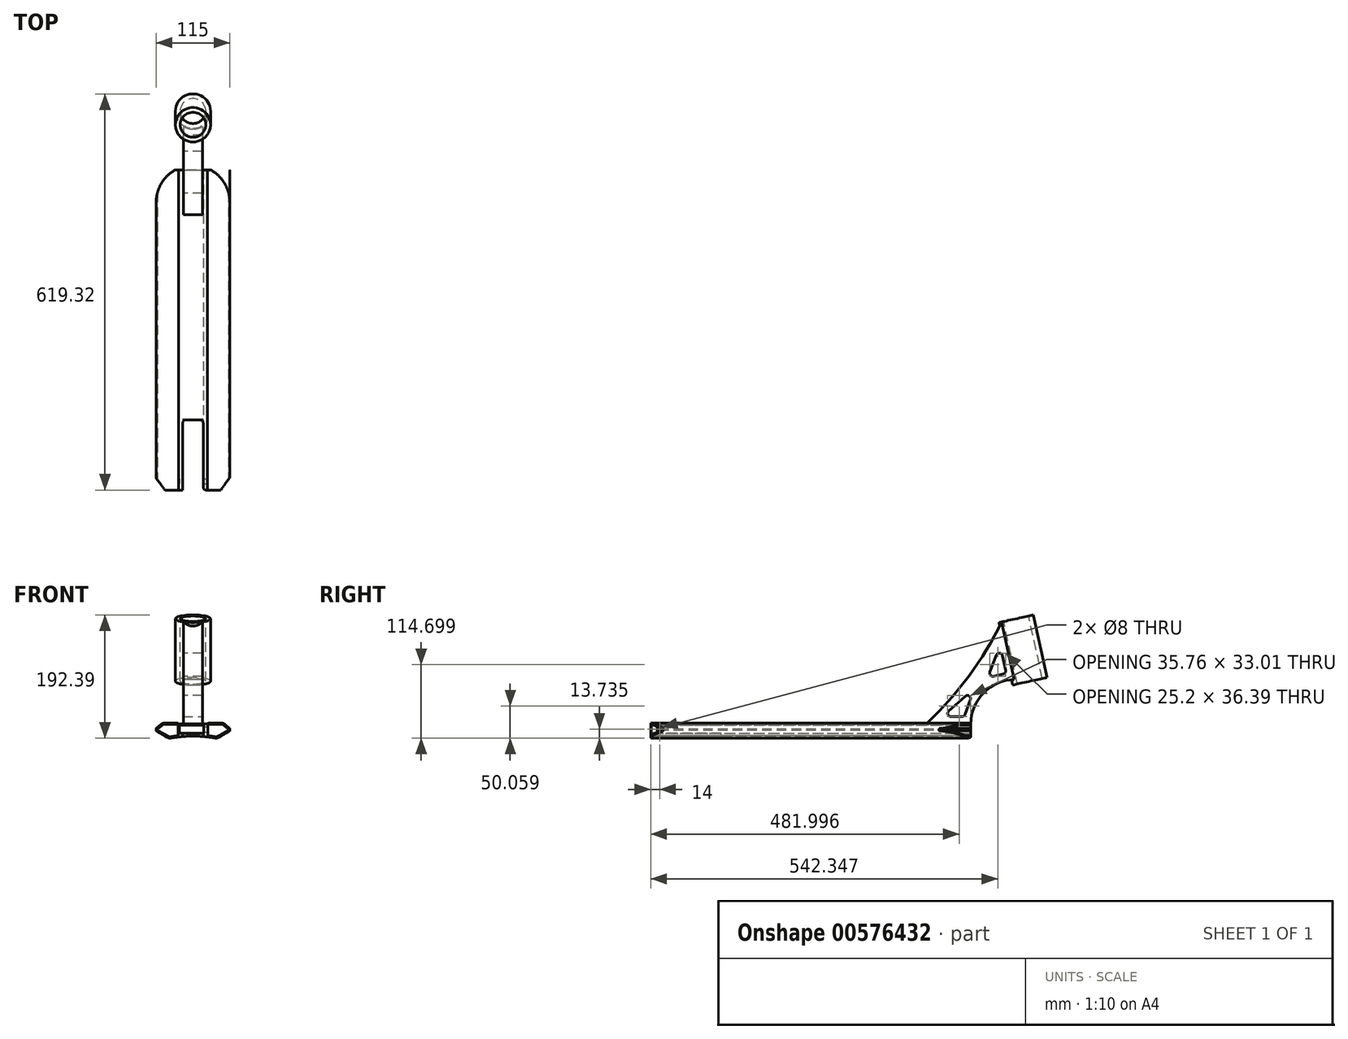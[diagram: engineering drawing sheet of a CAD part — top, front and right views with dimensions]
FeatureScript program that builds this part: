
annotation { "Feature Type Name" : "Feature", "Feature Type Description" : "" }
export const myFeature = defineFeature(function(context is Context, id is Id, definition is map)
    precondition{}
    {
        {
            var Q0;
            Q0=qCreatedBy(makeId("Front.planeOp"),FACE);
            var sketch = newSketch(context, id + "F0", { "sketchPlane" : qUnion([Q0])});
            skLineSegment(sketch, "E0", {"start": v(0, 30.17) * mm, "end": v(0, 3.52) * mm});
            skLineSegment(sketch, "E1", {"start": v(0, 21.17) * mm, "end": v(22.5, 21.17) * mm});
            skLineSegment(sketch, "E2", {"start": v(22.5, 21.17) * mm, "end": v(22.5, 22.47) * mm});
            skLineSegment(sketch, "E3", {"start": v(22.5, 22.47) * mm, "end": v(47.5, 22.47) * mm});
            skLineSegment(sketch, "E4", {"start": v(47.5, 22.47) * mm, "end": v(57.5, 14.08) * mm});
            skLineSegment(sketch, "E5", {"start": v(57.5, 14.08) * mm, "end": v(57.5, 10.08) * mm});
            skLineSegment(sketch, "E6", {"start": v(57.5, 10.08) * mm, "end": v(37.4, -1.53) * mm});
            skLineSegment(sketch, "E7.MirrorCS", {"start": v(0, 21.17) * mm, "end": v(-22.5, 21.17) * mm});
            skLineSegment(sketch, "E8.MirrorCS", {"start": v(-22.5, 22.47) * mm, "end": v(-47.5, 22.47) * mm});
            skLineSegment(sketch, "E9.MirrorCS", {"start": v(-47.5, 22.47) * mm, "end": v(-57.5, 14.08) * mm});
            skLineSegment(sketch, "E10.MirrorCS", {"start": v(-57.5, 14.08) * mm, "end": v(-57.5, 10.08) * mm});
            skLineSegment(sketch, "E11.MirrorCS", {"start": v(-57.5, 10.08) * mm, "end": v(-37.4, -1.53) * mm});
            skLineSegment(sketch, "E12.MirrorCS", {"start": v(-22.5, 21.17) * mm, "end": v(-22.5, 22.47) * mm});
            skArc(sketch, "E13", {"start": v(37.4, -1.53) * mm, "mid": v(0, 2) * mm, "end": v(-37.4, -1.53) * mm});
            skSolve(sketch);
        }
        {
            var Q0;
            Q0 = qSketchRegion(id + "F0", true);
            extrude(context, id + "F1", {"entities" : qUnion([Q0]), "endBound" : BoundingType.SYMMETRIC, "depth" : 500 * mm, "offsetDistance" : 25 * mm});
        }
        {
            var Q0;
            Q0=qCreatedBy(makeId("Front.planeOp"),FACE);
            var sketch = newSketch(context, id + "F2", { "sketchPlane" : qUnion([Q0])});
            skLineSegment(sketch, "E14.bottom", {"start": v(-21.27, 19.17) * mm, "end": v(16.73, 19.17) * mm});
            skLineSegment(sketch, "E14.top", {"start": v(-21.27, 6.17) * mm, "end": v(16.73, 6.17) * mm});
            skLineSegment(sketch, "E14.left", {"start": v(-21.27, 19.17) * mm, "end": v(-21.27, 6.17) * mm});
            skLineSegment(sketch, "E14.right", {"start": v(16.73, 19.17) * mm, "end": v(16.73, 6.17) * mm});
            skSolve(sketch);
        }
        {
            var Q0;
            Q0 = qSketchRegion(id + "F2", true);
            extrude(context, id + "F3", {"entities" : qUnion([Q0]), "operationType" : NewBodyOperationType.REMOVE, "endBound" : BoundingType.SYMMETRIC, "depth" : 500 * mm, "offsetDistance" : 25 * mm});
        }
        {
            var Q0;
            Q0=makeQuery(id+"F1.opExtrude","SWEPT_EDGE",EDGE,{"disambiguationData":[OSD([sQuery(id+"F0.wireOp",EDGE,"E8.MirrorCS"),sQuery(id+"F0.wireOp",EDGE,"E12.MirrorCS")])]});
            var Q1;
            Q1=makeQuery(id+"F1.opExtrude","SWEPT_EDGE",EDGE,{"disambiguationData":[OSD([sQuery(id+"F0.wireOp",EDGE,"E2"),sQuery(id+"F0.wireOp",EDGE,"E3")])]});
            fillet(context, id + "F4", {"entities" : qUnion([Q0, Q1]), "radius" : 5 * mm, "tangentPropagation" : true, "allowEdgeOverflow" : false});
        }
        {
            var Q0;
            Q0=makeQuery(id+"F1.opExtrude","SWEPT_EDGE",EDGE,{"disambiguationData":[OSD([sQuery(id+"F0.wireOp",EDGE,"E3"),sQuery(id+"F0.wireOp",EDGE,"E4")])]});
            var Q1;
            Q1=makeQuery(id+"F1.opExtrude","SWEPT_EDGE",EDGE,{"disambiguationData":[OSD([sQuery(id+"F0.wireOp",EDGE,"E8.MirrorCS"),sQuery(id+"F0.wireOp",EDGE,"E9.MirrorCS")])]});
            var Q2;
            Q2=makeQuery(id+"F1.opExtrude","SWEPT_EDGE",EDGE,{"disambiguationData":[OSD([sQuery(id+"F0.wireOp",EDGE,"E11.MirrorCS"),sQuery(id+"F0.wireOp",EDGE,"E13")])]});
            var Q3;
            Q3=makeQuery(id+"F1.opExtrude","SWEPT_EDGE",EDGE,{"disambiguationData":[OSD([sQuery(id+"F0.wireOp",EDGE,"E6"),sQuery(id+"F0.wireOp",EDGE,"E13")])]});
            fillet(context, id + "F5", {"entities" : qUnion([Q0, Q1, Q2, Q3]), "radius" : 9 * mm, "tangentPropagation" : true, "allowEdgeOverflow" : false});
        }
        {
            var Q0;
            Q0=makeQuery(id+"F1.opExtrude","SWEPT_EDGE",EDGE,{"disambiguationData":[OSD([sQuery(id+"F0.wireOp",EDGE,"E4"),sQuery(id+"F0.wireOp",EDGE,"E5")])]});
            var Q1;
            Q1=makeQuery(id+"F1.opExtrude","SWEPT_EDGE",EDGE,{"disambiguationData":[OSD([sQuery(id+"F0.wireOp",EDGE,"E5"),sQuery(id+"F0.wireOp",EDGE,"E6")])]});
            var Q2;
            Q2=makeQuery(id+"F1.opExtrude","SWEPT_EDGE",EDGE,{"disambiguationData":[OSD([sQuery(id+"F0.wireOp",EDGE,"E9.MirrorCS"),sQuery(id+"F0.wireOp",EDGE,"E10.MirrorCS")])]});
            var Q3;
            Q3=makeQuery(id+"F1.opExtrude","SWEPT_EDGE",EDGE,{"disambiguationData":[OSD([sQuery(id+"F0.wireOp",EDGE,"E10.MirrorCS"),sQuery(id+"F0.wireOp",EDGE,"E11.MirrorCS")])]});
            fillet(context, id + "F6", {"entities" : qUnion([Q0, Q1, Q2, Q3]), "radius" : 1 * mm, "tangentPropagation" : true, "allowEdgeOverflow" : false});
        }
        {
            var Q0;
            Q0=makeQuery(id+"F1.opExtrude","CAP_FACE",FACE,{"disambiguationData":[OSD([sQuery(id+"F0.wireOp",EDGE,"E1"),sQuery(id+"F0.wireOp",EDGE,"E2"),sQuery(id+"F0.wireOp",EDGE,"E3"),sQuery(id+"F0.wireOp",EDGE,"E4"),sQuery(id+"F0.wireOp",EDGE,"E5"),sQuery(id+"F0.wireOp",EDGE,"E6"),sQuery(id+"F0.wireOp",EDGE,"E7.MirrorCS"),sQuery(id+"F0.wireOp",EDGE,"E8.MirrorCS"),sQuery(id+"F0.wireOp",EDGE,"E9.MirrorCS"),sQuery(id+"F0.wireOp",EDGE,"E10.MirrorCS"),sQuery(id+"F0.wireOp",EDGE,"E11.MirrorCS"),sQuery(id+"F0.wireOp",EDGE,"E12.MirrorCS"),sQuery(id+"F0.wireOp",EDGE,"E13")])],"isStart":false});
            var sketch = newSketch(context, id + "F7", { "sketchPlane" : qUnion([Q0])});
            skArc(sketch, "E15.0", {"start": v(34.56, 1.02) * mm, "mid": v(0, 4) * mm, "end": v(-34.56, 1.02) * mm});
            skArc(sketch, "E15.1", {"start": v(-39.25, 1.86) * mm, "mid": v(-36.98, 1.03) * mm, "end": v(-34.56, 1.02) * mm});
            skLineSegment(sketch, "E15.2", {"start": v(-55.5, 11.24) * mm, "end": v(-39.25, 1.86) * mm});
            skLineSegment(sketch, "E15.3", {"start": v(-55.5, 13.15) * mm, "end": v(-55.5, 11.24) * mm});
            skArc(sketch, "E15.4", {"start": v(-23.27, 18.97) * mm, "mid": v(-24.36, 20.07) * mm, "end": v(-25.86, 20.47) * mm});
            skLineSegment(sketch, "E15.5", {"start": v(-25.86, 20.47) * mm, "end": v(-44.22, 20.47) * mm});
            skArc(sketch, "E15.6", {"start": v(-44.22, 20.47) * mm, "mid": v(-46.62, 20.05) * mm, "end": v(-48.72, 18.83) * mm});
            skLineSegment(sketch, "E15.7", {"start": v(-48.72, 18.83) * mm, "end": v(-55.5, 13.15) * mm});
            skLineSegment(sketch, "E16", {"start": v(-23.27, 18.97) * mm, "end": v(-23.27, 2.65) * mm});
            skLineSegment(sketch, "E17.MirrorCS", {"start": v(23.27, 18.97) * mm, "end": v(23.27, 2.65) * mm});
            skArc(sketch, "E18.MirrorCS", {"start": v(23.27, 18.97) * mm, "mid": v(24.36, 20.07) * mm, "end": v(25.86, 20.47) * mm});
            skLineSegment(sketch, "E19.MirrorCS", {"start": v(25.86, 20.47) * mm, "end": v(44.22, 20.47) * mm});
            skArc(sketch, "E20.MirrorCS", {"start": v(44.22, 20.47) * mm, "mid": v(46.62, 20.05) * mm, "end": v(48.72, 18.83) * mm});
            skLineSegment(sketch, "E21.MirrorCS", {"start": v(48.72, 18.83) * mm, "end": v(55.5, 13.15) * mm});
            skLineSegment(sketch, "E22.MirrorCS", {"start": v(55.5, 13.15) * mm, "end": v(55.5, 11.24) * mm});
            skLineSegment(sketch, "E23.MirrorCS", {"start": v(55.5, 11.24) * mm, "end": v(39.25, 1.86) * mm});
            skArc(sketch, "E24.MirrorCS", {"start": v(39.25, 1.86) * mm, "mid": v(36.98, 1.03) * mm, "end": v(34.56, 1.02) * mm});
            skArc(sketch, "E25.MirrorCS", {"start": v(-34.56, 1.02) * mm, "mid": v(0, 4) * mm, "end": v(34.56, 1.02) * mm});
            skSolve(sketch);
        }
        {
            var Q0;
            {var subQ0=sQuery(id+"F7.wireOp",EDGE,"E15.1");Q0=makeQuery(id+"F7.imprint","IMPRINT",FACE,{"disambiguationData":[TD([[makeQuery(id+"F7.imprint","IMPRINT",EDGE,{"derivedFrom":subQ0}),1.0]])]});}
            var Q1;
            {var subQ0=sQuery(id+"F7.wireOp",EDGE,"E17.MirrorCS");Q1=makeQuery(id+"F7.imprint","IMPRINT",FACE,{"disambiguationData":[TD([[makeQuery(id+"F7.imprint","IMPRINT",EDGE,{"derivedFrom":subQ0}),1.0]])]});}
            extrude(context, id + "F8", {"entities" : qUnion([Q0, Q1]), "operationType" : NewBodyOperationType.REMOVE, "endBound" : BoundingType.THROUGH_ALL, "oppositeDirection" : true, "depth" : 25 * mm, "offsetDistance" : 25 * mm});
        }
        {
            var Q0;
            Q0=qCreatedBy(makeId("Top.planeOp"),FACE);
            var sketch = newSketch(context, id + "F9", { "sketchPlane" : qUnion([Q0])});
            skArc(sketch, "E26", {"start": v(57.5, 200.26) * mm, "mid": v(-0.46, 257.5) * mm, "end": v(-57.5, 199.33) * mm});
            skLineSegment(sketch, "E27", {"start": v(-57.5, 199.33) * mm, "end": v(-57.5, 280.26) * mm});
            skLineSegment(sketch, "E28", {"start": v(-57.5, 280.26) * mm, "end": v(57.14, 280.26) * mm});
            skLineSegment(sketch, "E29", {"start": v(57.14, 280.26) * mm, "end": v(57.5, 200.26) * mm});
            skSolve(sketch);
        }
        {
            var Q0;
            {var subQ0=sQuery(id+"F9.wireOp",EDGE,"E27");var subQ1=sQuery(id+"F9.wireOp",EDGE,"E26");var subQ2=makeQuery(id+"F9.imprint","INTERSECT",VERTEX,{"disambiguationData":[OD(0.0)],"derivedFrom":[subQ1,subQ0]});Q0=makeQuery(id+"F9.imprint","IMPRINT",FACE,{"disambiguationData":[TD([[makeQuery(id+"F9.imprint","IMPRINT",EDGE,{"disambiguationData":[TD([[subQ2,1.0]])],"derivedFrom":subQ1}),1.0]])]});}
            var Q1;
            {var subQ4=sQuery(id+"F9.wireOp",EDGE,"E28");Q1=makeQuery(id+"F9.imprint","IMPRINT",FACE,{"disambiguationData":[TD([[makeQuery(id+"F9.imprint","IMPRINT",EDGE,{"derivedFrom":subQ4}),-1.0]])]});}
            extrude(context, id + "F10", {"entities" : qUnion([Q0, Q1]), "operationType" : NewBodyOperationType.REMOVE, "endBound" : BoundingType.THROUGH_ALL, "oppositeDirection" : true, "depth" : 25 * mm, "offsetDistance" : 25 * mm, "hasSecondDirection" : true, "secondDirectionBound" : SecondDirectionBoundingType.THROUGH_ALL, "secondDirectionOppositeDirection" : false, "secondDirectionDepth" : 25 * mm});
        }
        {
            var Q0;
            Q0=qCreatedBy(makeId("Top.planeOp"),FACE);
            var sketch = newSketch(context, id + "F11", { "sketchPlane" : qUnion([Q0])});
            skLineSegment(sketch, "E30", {"start": v(-68, -346) * mm, "end": v(68, -346) * mm});
            skLineSegment(sketch, "E31", {"start": v(68, -346) * mm, "end": v(68, -216) * mm});
            skLineSegment(sketch, "E32", {"start": v(68, -216) * mm, "end": v(43.3, -250) * mm});
            skLineSegment(sketch, "E33", {"start": v(43.3, -250) * mm, "end": v(16, -250) * mm});
            skLineSegment(sketch, "E34", {"start": v(16, -250) * mm, "end": v(16, -140) * mm});
            skLineSegment(sketch, "E35", {"start": v(16, -140) * mm, "end": v(-16, -140) * mm});
            skLineSegment(sketch, "E36", {"start": v(-16, -140) * mm, "end": v(-16, -250) * mm});
            skLineSegment(sketch, "E37", {"start": v(-16, -250) * mm, "end": v(-43.77, -250) * mm});
            skLineSegment(sketch, "E38", {"start": v(-43.77, -250) * mm, "end": v(-68.78, -216) * mm});
            skLineSegment(sketch, "E39", {"start": v(-68.78, -216) * mm, "end": v(-68, -346) * mm});
            skSolve(sketch);
        }
        {
            var Q0;
            Q0 = qSketchRegion(id + "F11", true);
            extrude(context, id + "F12", {"entities" : qUnion([Q0]), "operationType" : NewBodyOperationType.REMOVE, "endBound" : BoundingType.THROUGH_ALL, "oppositeDirection" : true, "depth" : 25 * mm, "offsetDistance" : 25 * mm, "hasSecondDirection" : true, "secondDirectionBound" : SecondDirectionBoundingType.THROUGH_ALL, "secondDirectionOppositeDirection" : false, "secondDirectionDepth" : 25 * mm});
        }
        {
            var Q0;
            {var subQ0=sQuery(id+"F0.wireOp",EDGE,"E13");var subQ1=sQuery(id+"F11.wireOp",EDGE,"E36");Q0=makeQuery(id+"F12.boolean.opBoolean","COPY",EDGE,{"disambiguationData":[TD([makeQuery(id+"F1.opExtrude","SWEPT_FACE",FACE,{"disambiguationData":[OSD([subQ0])]})])],"derivedFrom":makeQuery(id+"F12.opExtrude","SWEPT_EDGE",EDGE,{"disambiguationData":[OSD([subQ1,sQuery(id+"F11.wireOp",EDGE,"E37")])]})});}
            var Q1;
            {var subQ2=sQuery(id+"F11.wireOp",EDGE,"E36");Q1=makeQuery(id+"F12.boolean.opBoolean","COPY",EDGE,{"disambiguationData":[TD([makeQuery(id+"F3.boolean.opBoolean","COPY",FACE,{"derivedFrom":makeQuery(id+"F3.opExtrude","SWEPT_FACE",FACE,{"disambiguationData":[OSD([sQuery(id+"F2.wireOp",EDGE,"E14.bottom")])]})})])],"derivedFrom":makeQuery(id+"F12.opExtrude","SWEPT_EDGE",EDGE,{"disambiguationData":[OSD([subQ2,sQuery(id+"F11.wireOp",EDGE,"E37")])]})});}
            var Q2;
            {var subQ0=sQuery(id+"F11.wireOp",EDGE,"E35");var subQ1=sQuery(id+"F11.wireOp",EDGE,"E36");Q2=makeQuery(id+"F12.boolean.opBoolean","COPY",EDGE,{"disambiguationData":[TD([makeQuery(id+"F3.boolean.opBoolean","COPY",FACE,{"derivedFrom":makeQuery(id+"F3.opExtrude","SWEPT_FACE",FACE,{"disambiguationData":[OSD([sQuery(id+"F2.wireOp",EDGE,"E14.bottom")])]})})])],"derivedFrom":makeQuery(id+"F12.opExtrude","SWEPT_EDGE",EDGE,{"disambiguationData":[OSD([subQ0,subQ1])]})});}
            var Q3;
            {var subQ2=sQuery(id+"F11.wireOp",EDGE,"E34");Q3=makeQuery(id+"F12.boolean.opBoolean","COPY",EDGE,{"disambiguationData":[TD([makeQuery(id+"F3.boolean.opBoolean","COPY",FACE,{"derivedFrom":makeQuery(id+"F3.opExtrude","SWEPT_FACE",FACE,{"disambiguationData":[OSD([sQuery(id+"F2.wireOp",EDGE,"E14.bottom")])]})})])],"derivedFrom":makeQuery(id+"F12.opExtrude","SWEPT_EDGE",EDGE,{"disambiguationData":[OSD([sQuery(id+"F11.wireOp",EDGE,"E33"),subQ2])]})});}
            var Q4;
            {var subQ0=sQuery(id+"F11.wireOp",EDGE,"E35");var subQ1=sQuery(id+"F11.wireOp",EDGE,"E34");Q4=makeQuery(id+"F12.boolean.opBoolean","COPY",EDGE,{"disambiguationData":[TD([makeQuery(id+"F3.boolean.opBoolean","COPY",FACE,{"derivedFrom":makeQuery(id+"F3.opExtrude","SWEPT_FACE",FACE,{"disambiguationData":[OSD([sQuery(id+"F2.wireOp",EDGE,"E14.bottom")])]})})])],"derivedFrom":makeQuery(id+"F12.opExtrude","SWEPT_EDGE",EDGE,{"disambiguationData":[OSD([subQ1,subQ0])]})});}
            var Q5;
            {var subQ0=sQuery(id+"F0.wireOp",EDGE,"E13");var subQ1=sQuery(id+"F11.wireOp",EDGE,"E34");Q5=makeQuery(id+"F12.boolean.opBoolean","COPY",EDGE,{"disambiguationData":[TD([makeQuery(id+"F1.opExtrude","SWEPT_FACE",FACE,{"disambiguationData":[OSD([subQ0])]})])],"derivedFrom":makeQuery(id+"F12.opExtrude","SWEPT_EDGE",EDGE,{"disambiguationData":[OSD([sQuery(id+"F11.wireOp",EDGE,"E33"),subQ1])]})});}
            fillet(context, id + "F13", {"entities" : qUnion([Q0, Q1, Q2, Q3, Q4, Q5]), "radius" : 5 * mm, "tangentPropagation" : true, "allowEdgeOverflow" : false});
        }
        {
            var Q0;
            Q0=qCreatedBy(makeId("Right.planeOp"),FACE);
            var sketch = newSketch(context, id + "F14", { "sketchPlane" : qUnion([Q0])});
            skLineSegment(sketch, "E40", {"start": v(180, 20.47) * mm, "end": v(250, 20.47) * mm});
            skArc(sketch, "E41", {"start": v(318.32, 90.45) * mm, "mid": v(269.91, 69.37) * mm, "end": v(250, 20.47) * mm});
            skLineSegment(sketch, "E42", {"start": v(318.32, 90.45) * mm, "end": v(320, 82.8) * mm});
            skLineSegment(sketch, "E43", {"start": v(320, 82.8) * mm, "end": v(364.93, 92.68) * mm});
            skLineSegment(sketch, "E44", {"start": v(364.93, 92.68) * mm, "end": v(343.47, 190.35) * mm});
            skLineSegment(sketch, "E45", {"start": v(343.47, 190.35) * mm, "end": v(298.54, 180.47) * mm});
            skArc(sketch, "E46", {"start": v(180, 20.47) * mm, "mid": v(246.57, 95.06) * mm, "end": v(298.54, 180.47) * mm});
            skSolve(sketch);
        }
        {
            var Q0;
            Q0 = qSketchRegion(id + "F14", true);
            extrude(context, id + "F15", {"entities" : qUnion([Q0]), "operationType" : NewBodyOperationType.ADD, "endBound" : BoundingType.SYMMETRIC, "depth" : 30 * mm, "offsetDistance" : 25 * mm});
        }
        {
            var Q0;
            Q0=makeQuery(id+"F15.opExtrude","SWEPT_FACE",FACE,{"disambiguationData":[OSD([sQuery(id+"F14.wireOp",EDGE,"E45")])]});
            var sketch = newSketch(context, id + "F16", { "sketchPlane" : qUnion([Q0])});
            skCircle(sketch, "E47", {"center": v(0, 353.31) * mm, "radius": 27.5 * mm});
            skSolve(sketch);
        }
        {
            var Q0;
            Q0 = qSketchRegion(id + "F16", true);
            var Q1;
            Q1=makeQuery(id+"F15.opExtrude","SWEPT_FACE",FACE,{"disambiguationData":[OSD([sQuery(id+"F14.wireOp",EDGE,"E43")])]});
            extrude(context, id + "F17", {"entities" : qUnion([Q0]), "operationType" : NewBodyOperationType.ADD, "endBound" : BoundingType.UP_TO_SURFACE, "oppositeDirection" : true, "depth" : 25 * mm, "endBoundEntityFace" : qUnion([Q1]), "offsetDistance" : 25 * mm});
        }
        {
            var Q0;
            Q0=makeQuery(id+"F17.boolean.opBoolean","MERGE",FACE,{"derivedFrom":[makeQuery(id+"F15.opExtrude","SWEPT_FACE",FACE,{"disambiguationData":[OSD([sQuery(id+"F14.wireOp",EDGE,"E45")])]}),makeQuery(id+"F17.opExtrude","CAP_FACE",FACE,{"disambiguationData":[OSD([sQuery(id+"F16.wireOp",EDGE,"E47")])],"isStart":true})]});
            var sketch = newSketch(context, id + "F18", { "sketchPlane" : qUnion([Q0])});
            skPoint(sketch, "E48", {"position": v(0, 353.31) * mm});
            skSolve(sketch);
        }
        {
            var Q0;
            Q0=sQuery(id+"F18.wireOp",VERTEX,"E48");
            var Q1;
            Q1=makeQuery(id+"F1.opExtrude","SWEPT_BODY",BODY,{"disambiguationData":[OSD([sQuery(id+"F0.wireOp",EDGE,"E1"),sQuery(id+"F0.wireOp",EDGE,"E2"),sQuery(id+"F0.wireOp",EDGE,"E3"),sQuery(id+"F0.wireOp",EDGE,"E4"),sQuery(id+"F0.wireOp",EDGE,"E5"),sQuery(id+"F0.wireOp",EDGE,"E6"),sQuery(id+"F0.wireOp",EDGE,"E7.MirrorCS"),sQuery(id+"F0.wireOp",EDGE,"E8.MirrorCS"),sQuery(id+"F0.wireOp",EDGE,"E9.MirrorCS"),sQuery(id+"F0.wireOp",EDGE,"E10.MirrorCS"),sQuery(id+"F0.wireOp",EDGE,"E11.MirrorCS"),sQuery(id+"F0.wireOp",EDGE,"E12.MirrorCS"),sQuery(id+"F0.wireOp",EDGE,"E13")])]});
            hole(context, id + "F19", {"style" : HoleStyle.SIMPLE, "endStyle" : HoleEndStyle.THROUGH, "holeDiameter" : 40 * mm, "majorDiameter" : 5 * mm, "isTappedThrough" : true, "tappedDepth" : 12 * mm, "tapClearance" : 3, "locations" : qUnion([Q0]), "scope" : qUnion([Q1])});
        }
        {
            var Q0;
            Q0=makeQuery(id+"F8.boolean.opBoolean","COPY",FACE,{"derivedFrom":makeQuery(id+"F8.opExtrude","SWEPT_FACE",FACE,{"disambiguationData":[OSD([sQuery(id+"F7.wireOp",EDGE,"E17.MirrorCS")])]})});
            var sketch = newSketch(context, id + "F20", { "sketchPlane" : qUnion([Q0])});
            skPoint(sketch, "E49", {"position": v(-236, 12.65) * mm});
            skSolve(sketch);
        }
        {
            var Q0;
            Q0=sQuery(id+"F20.wireOp",VERTEX,"E49");
            var Q1;
            Q1=makeQuery(id+"F1.opExtrude","SWEPT_BODY",BODY,{"disambiguationData":[OSD([sQuery(id+"F0.wireOp",EDGE,"E1"),sQuery(id+"F0.wireOp",EDGE,"E2"),sQuery(id+"F0.wireOp",EDGE,"E3"),sQuery(id+"F0.wireOp",EDGE,"E4"),sQuery(id+"F0.wireOp",EDGE,"E5"),sQuery(id+"F0.wireOp",EDGE,"E6"),sQuery(id+"F0.wireOp",EDGE,"E7.MirrorCS"),sQuery(id+"F0.wireOp",EDGE,"E8.MirrorCS"),sQuery(id+"F0.wireOp",EDGE,"E9.MirrorCS"),sQuery(id+"F0.wireOp",EDGE,"E10.MirrorCS"),sQuery(id+"F0.wireOp",EDGE,"E11.MirrorCS"),sQuery(id+"F0.wireOp",EDGE,"E12.MirrorCS"),sQuery(id+"F0.wireOp",EDGE,"E13")])]});
            hole(context, id + "F21", {"style" : HoleStyle.SIMPLE, "endStyle" : HoleEndStyle.BLIND, "holeDiameter" : 8 * mm, "majorDiameter" : 5 * mm, "holeDepth" : 55 * mm, "isTappedThrough" : true, "tappedDepth" : 12 * mm, "tapClearance" : 3, "locations" : qUnion([Q0]), "scope" : qUnion([Q1])});
        }
        {
            var Q0;
            Q0=makeQuery(id+"F15.opExtrude","CAP_FACE",FACE,{"disambiguationData":[OSD([sQuery(id+"F14.wireOp",EDGE,"E40"),sQuery(id+"F14.wireOp",EDGE,"E41"),sQuery(id+"F14.wireOp",EDGE,"E42"),sQuery(id+"F14.wireOp",EDGE,"E43"),sQuery(id+"F14.wireOp",EDGE,"E44"),sQuery(id+"F14.wireOp",EDGE,"E45"),sQuery(id+"F14.wireOp",EDGE,"E46")])],"isStart":false});
            var sketch = newSketch(context, id + "F22", { "sketchPlane" : qUnion([Q0])});
            skLineSegment(sketch, "E50", {"start": v(276.66, 93.42) * mm, "end": v(305.9, 100.18) * mm});
            skLineSegment(sketch, "E51", {"start": v(305.9, 100.18) * mm, "end": v(296.23, 144.13) * mm});
            skLineSegment(sketch, "E52", {"start": v(296.23, 144.13) * mm, "end": v(276.66, 93.42) * mm});
            skLineSegment(sketch, "E53", {"start": v(206, 32.47) * mm, "end": v(240, 32.47) * mm});
            skLineSegment(sketch, "E54", {"start": v(240, 32.47) * mm, "end": v(256.38, 77.47) * mm});
            skLineSegment(sketch, "E55", {"start": v(256.38, 77.47) * mm, "end": v(206, 32.47) * mm});
            skSolve(sketch);
        }
        {
            var Q0;
            Q0=makeQuery(id+"F22.imprint","IMPRINT",FACE,{"disambiguationData":[TD([[makeQuery(id+"F22.imprint","IMPRINT",EDGE,{"derivedFrom":sQuery(id+"F22.wireOp",EDGE,"E53")}),1.0]])]});
            var Q1;
            Q1=makeQuery(id+"F22.imprint","IMPRINT",FACE,{"disambiguationData":[TD([[makeQuery(id+"F22.imprint","IMPRINT",EDGE,{"derivedFrom":sQuery(id+"F22.wireOp",EDGE,"E50")}),1.0]])]});
            extrude(context, id + "F23", {"entities" : qUnion([Q0, Q1]), "operationType" : NewBodyOperationType.REMOVE, "endBound" : BoundingType.THROUGH_ALL, "oppositeDirection" : true, "depth" : 25 * mm, "offsetDistance" : 25 * mm});
        }
        {
            var Q0;
            Q0=makeQuery(id+"F23.boolean.opBoolean","COPY",EDGE,{"derivedFrom":makeQuery(id+"F23.opExtrude","SWEPT_EDGE",EDGE,{"disambiguationData":[OSD([sQuery(id+"F22.wireOp",EDGE,"E53"),sQuery(id+"F22.wireOp",EDGE,"E55")])]})});
            var Q1;
            Q1=makeQuery(id+"F23.boolean.opBoolean","COPY",EDGE,{"derivedFrom":makeQuery(id+"F23.opExtrude","SWEPT_EDGE",EDGE,{"disambiguationData":[OSD([sQuery(id+"F22.wireOp",EDGE,"E54"),sQuery(id+"F22.wireOp",EDGE,"E55")])]})});
            var Q2;
            Q2=makeQuery(id+"F23.boolean.opBoolean","COPY",EDGE,{"derivedFrom":makeQuery(id+"F23.opExtrude","SWEPT_EDGE",EDGE,{"disambiguationData":[OSD([sQuery(id+"F22.wireOp",EDGE,"E53"),sQuery(id+"F22.wireOp",EDGE,"E54")])]})});
            var Q3;
            Q3=makeQuery(id+"F23.boolean.opBoolean","COPY",EDGE,{"derivedFrom":makeQuery(id+"F23.opExtrude","SWEPT_EDGE",EDGE,{"disambiguationData":[OSD([sQuery(id+"F22.wireOp",EDGE,"E50"),sQuery(id+"F22.wireOp",EDGE,"E52")])]})});
            var Q4;
            Q4=makeQuery(id+"F23.boolean.opBoolean","COPY",EDGE,{"derivedFrom":makeQuery(id+"F23.opExtrude","SWEPT_EDGE",EDGE,{"disambiguationData":[OSD([sQuery(id+"F22.wireOp",EDGE,"E50"),sQuery(id+"F22.wireOp",EDGE,"E51")])]})});
            var Q5;
            Q5=makeQuery(id+"F23.boolean.opBoolean","COPY",EDGE,{"derivedFrom":makeQuery(id+"F23.opExtrude","SWEPT_EDGE",EDGE,{"disambiguationData":[OSD([sQuery(id+"F22.wireOp",EDGE,"E51"),sQuery(id+"F22.wireOp",EDGE,"E52")])]})});
            fillet(context, id + "F24", {"entities" : qUnion([Q0, Q1, Q2, Q3, Q4, Q5]), "radius" : 5 * mm, "tangentPropagation" : true, "allowEdgeOverflow" : false});
        }
    });
